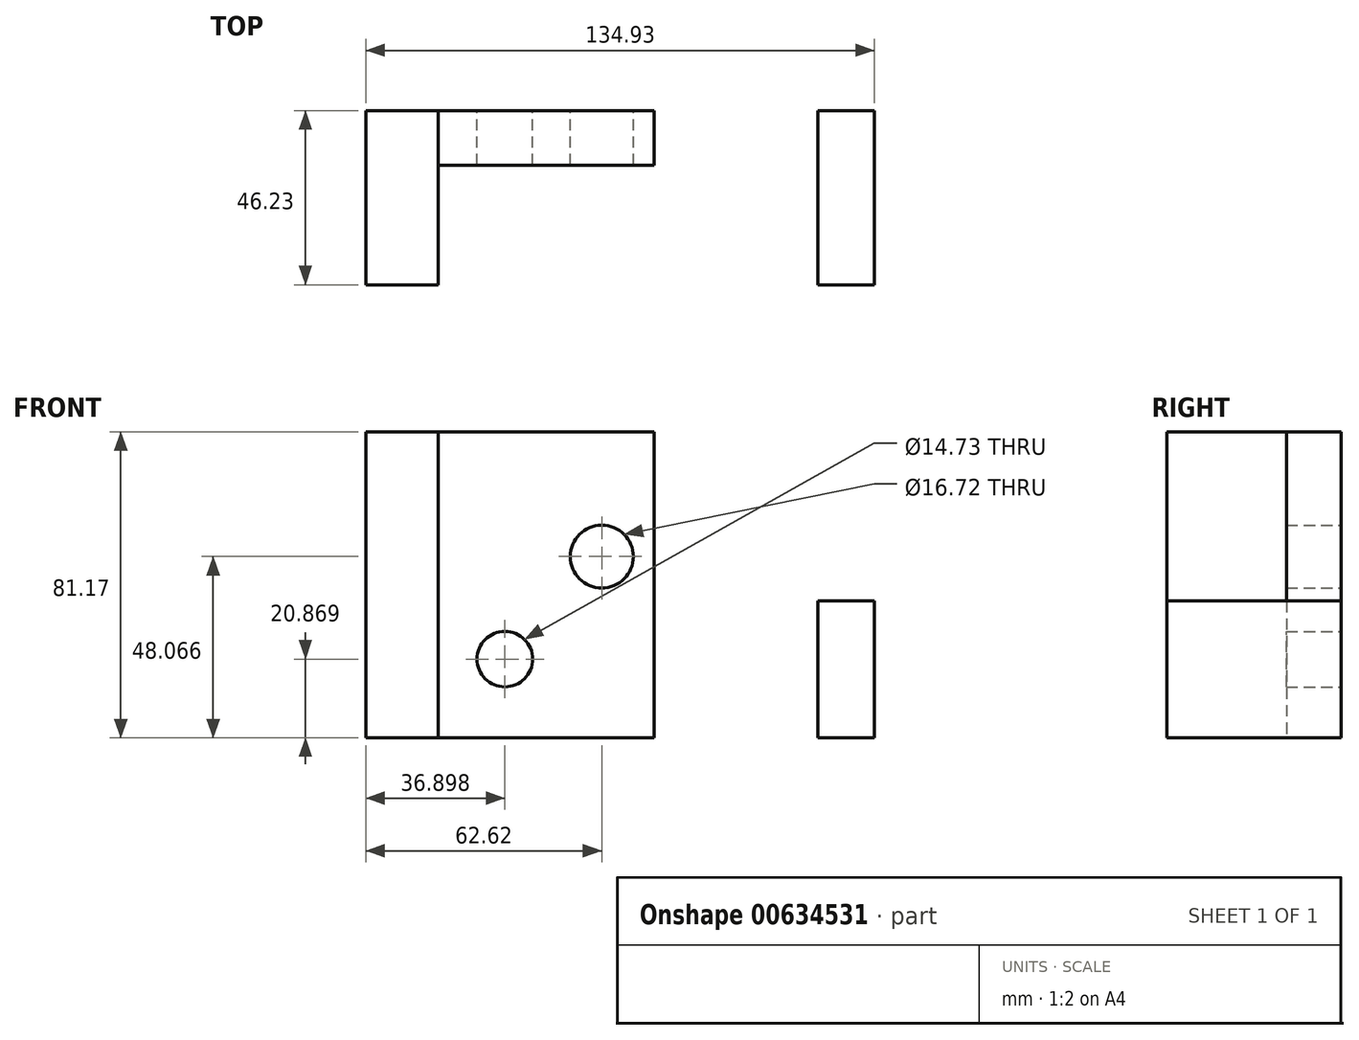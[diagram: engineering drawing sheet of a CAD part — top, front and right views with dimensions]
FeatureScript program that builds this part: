
annotation { "Feature Type Name" : "Feature", "Feature Type Description" : "" }
export const myFeature = defineFeature(function(context is Context, id is Id, definition is map)
    precondition{}
    {
        {
            var Q0;
            Q0=qCreatedBy(makeId("Front.planeOp"),FACE);
            var sketch = newSketch(context, id + "F0", { "sketchPlane" : qUnion([Q0])});
            skLineSegment(sketch, "E0.bottom", {"start": v(-58.93, 44.9) * mm, "end": v(17.6, 44.9) * mm});
            skLineSegment(sketch, "E0.top", {"start": v(-58.93, -36.26) * mm, "end": v(17.6, -36.26) * mm});
            skLineSegment(sketch, "E0.left", {"start": v(-58.93, 44.9) * mm, "end": v(-58.93, -36.26) * mm});
            skLineSegment(sketch, "E0.right", {"start": v(17.6, 44.9) * mm, "end": v(17.6, -36.26) * mm});
            skLineSegment(sketch, "E1.bottom", {"start": v(17.6, -36.26) * mm, "end": v(76, -36.26) * mm});
            skLineSegment(sketch, "E1.top", {"start": v(17.6, 0) * mm, "end": v(76, 0) * mm});
            skLineSegment(sketch, "E1.left", {"start": v(17.6, -36.26) * mm, "end": v(17.6, 0) * mm});
            skLineSegment(sketch, "E1.right", {"start": v(76, -36.26) * mm, "end": v(76, 0) * mm});
            skLineSegment(sketch, "E2", {"start": v(-39.74, 44.9) * mm, "end": v(-39.74, -36.26) * mm});
            skLineSegment(sketch, "E3", {"start": v(61.04, 0) * mm, "end": v(61.04, -36.26) * mm});
            skCircle(sketch, "E4", {"center": v(-22.03, -15.4) * mm, "radius": 7.36 * mm});
            skCircle(sketch, "E5", {"center": v(3.69, 11.8) * mm, "radius": 8.36 * mm});
            skSolve(sketch);
        }
        {
            var Q0;
            {var subQ0=sQuery(id+"F0.wireOp",EDGE,"E0.left");Q0=makeQuery(id+"F0.imprint","IMPRINT",FACE,{"disambiguationData":[TD([[makeQuery(id+"F0.imprint","IMPRINT",EDGE,{"derivedFrom":subQ0}),1.0]])]});}
            var Q1;
            {var subQ0=sQuery(id+"F0.wireOp",EDGE,"E1.right");Q1=makeQuery(id+"F0.imprint","IMPRINT",FACE,{"disambiguationData":[TD([[makeQuery(id+"F0.imprint","IMPRINT",EDGE,{"derivedFrom":subQ0}),1.0]])]});}
            extrude(context, id + "F1", {"entities" : qUnion([Q0, Q1]), "depth" : 46.23 * mm, "offsetDistance" : 25.4 * mm});
        }
        {
            var Q0;
            {var subQ0=sQuery(id+"F0.wireOp",EDGE,"E1.left");Q0=makeQuery(id+"F0.imprint","IMPRINT",FACE,{"disambiguationData":[TD([[makeQuery(id+"F0.imprint","IMPRINT",EDGE,{"derivedFrom":subQ0}),-1.0]])]});}
            var Q1;
            {var subQ1=sQuery(id+"F0.wireOp",EDGE,"E0.right");Q1=makeQuery(id+"F0.imprint","IMPRINT",FACE,{"disambiguationData":[TD([[makeQuery(id+"F0.imprint","IMPRINT",EDGE,{"derivedFrom":subQ1}),-1.0]])]});}
            extrude(context, id + "F2", {"entities" : qUnion([Q0, Q1]), "depth" : 14.48 * mm, "offsetDistance" : 25.4 * mm});
        }
    });
